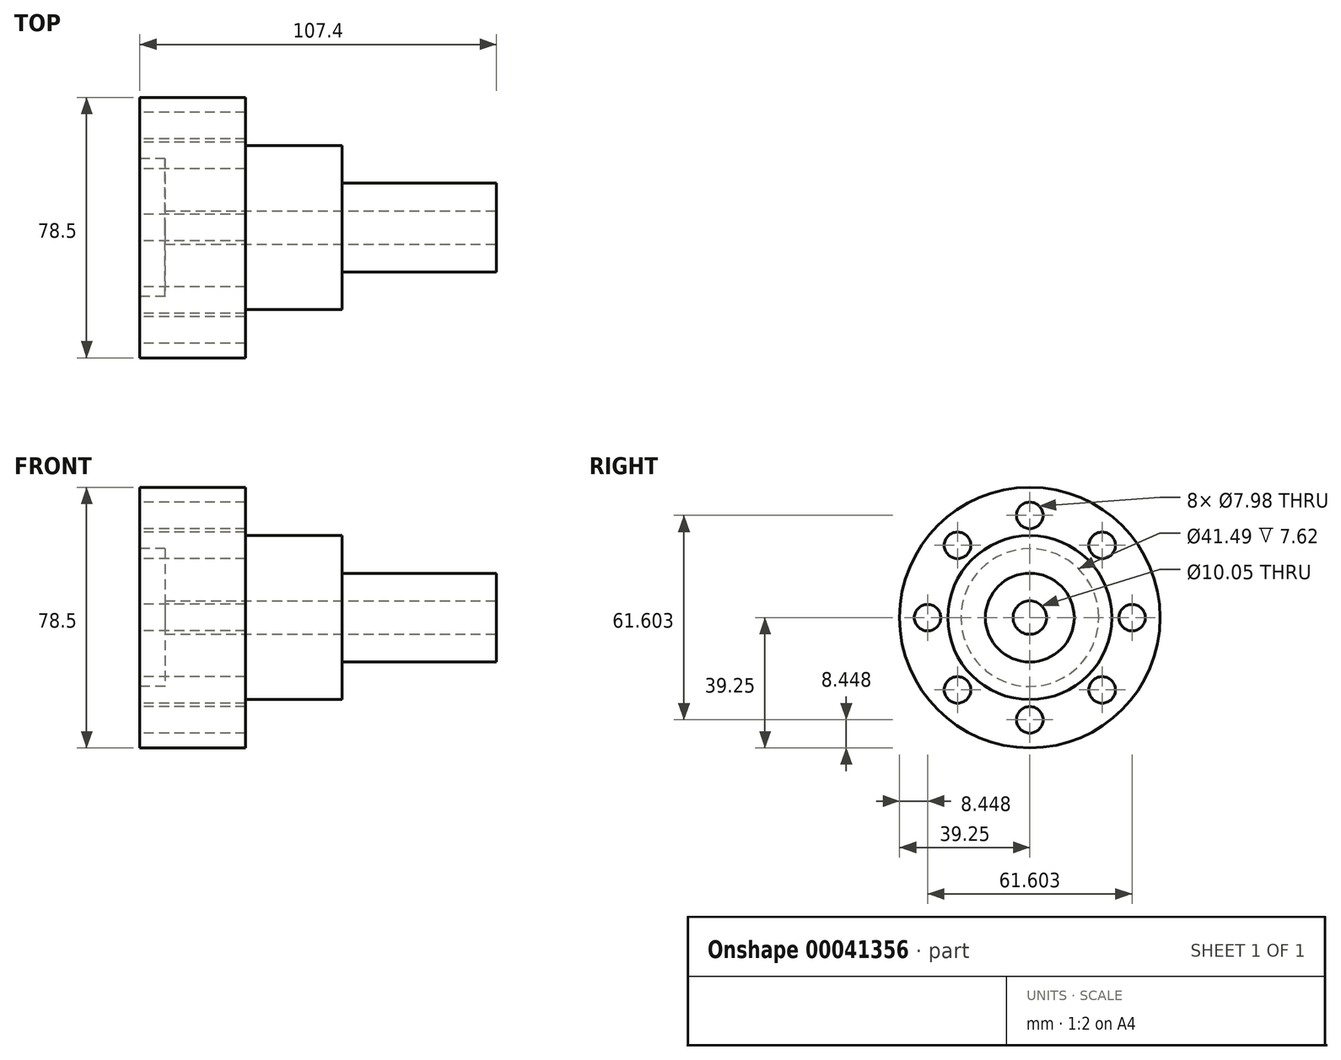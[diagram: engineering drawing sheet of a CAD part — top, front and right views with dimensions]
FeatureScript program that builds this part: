
annotation { "Feature Type Name" : "Feature", "Feature Type Description" : "" }
export const myFeature = defineFeature(function(context is Context, id is Id, definition is map)
    precondition{}
    {
        {
            var Q0;
            Q0=qCreatedBy(makeId("Front.planeOp"),FACE);
            var sketch = newSketch(context, id + "F0", { "sketchPlane" : qUnion([Q0])});
            skLineSegment(sketch, "E0", {"start": v(0, 0) * mm, "end": v(0, 39.25) * mm});
            skLineSegment(sketch, "E1", {"start": v(0, 39.25) * mm, "end": v(31.8, 39.25) * mm});
            skLineSegment(sketch, "E2", {"start": v(31.8, 39.25) * mm, "end": v(31.8, 24.7) * mm});
            skLineSegment(sketch, "E3", {"start": v(31.8, 24.7) * mm, "end": v(60.91, 24.7) * mm});
            skLineSegment(sketch, "E4", {"start": v(60.91, 24.7) * mm, "end": v(60.91, 13.38) * mm});
            skLineSegment(sketch, "E5", {"start": v(60.91, 13.38) * mm, "end": v(107.4, 13.38) * mm});
            skLineSegment(sketch, "E6", {"start": v(107.4, 13.38) * mm, "end": v(107.4, 0) * mm});
            skLineSegment(sketch, "E7", {"start": v(107.4, 0) * mm, "end": v(0, 0) * mm});
            skSolve(sketch);
        }
        {
            var Q0;
            Q0=makeQuery(id+"F0.imprint","IMPRINT",FACE,{"disambiguationData":[TD([[makeQuery(id+"F0.imprint","IMPRINT",EDGE,{"derivedFrom":sQuery(id+"F0.wireOp",EDGE,"E0")}),-1.0]])]});
            var Q1;
            Q1=sQuery(id+"F0.wireOp",EDGE,"E7");
            revolve(context, id + "F1", {"entities" : qUnion([Q0]), "axis" : qUnion([Q1]), "revolveType" : RevolveType.FULL});
        }
        {
            var Q0;
            Q0=makeQuery(id+"F1.opRevolve","SWEPT_FACE",FACE,{"disambiguationData":[OSD([sQuery(id+"F0.wireOp",EDGE,"E0")])]});
            var sketch = newSketch(context, id + "F2", { "sketchPlane" : qUnion([Q0])});
            skCircle(sketch, "E8", {"center": v(0, 0) * mm, "radius": 20.75 * mm});
            skSolve(sketch);
        }
        {
            var Q0;
            Q0=makeQuery(id+"F2.imprint","IMPRINT",FACE,{"disambiguationData":[TD([[makeQuery(id+"F2.imprint","IMPRINT",EDGE,{"derivedFrom":sQuery(id+"F2.wireOp",EDGE,"E8")}),1.0]])]});
            extrude(context, id + "F3", {"entities" : qUnion([Q0]), "operationType" : NewBodyOperationType.REMOVE, "oppositeDirection" : true, "depth" : 7.62 * mm});
        }
        {
            var Q0;
            Q0=makeQuery(id+"F1.opRevolve","SWEPT_FACE",FACE,{"disambiguationData":[OSD([sQuery(id+"F0.wireOp",EDGE,"E6")])]});
            var sketch = newSketch(context, id + "F4", { "sketchPlane" : qUnion([Q0])});
            skCircle(sketch, "E9", {"center": v(0, 0) * mm, "radius": 5.03 * mm});
            skSolve(sketch);
        }
        {
            var Q0;
            Q0=makeQuery(id+"F4.imprint","IMPRINT",FACE,{"disambiguationData":[TD([[makeQuery(id+"F4.imprint","IMPRINT",EDGE,{"derivedFrom":sQuery(id+"F4.wireOp",EDGE,"E9")}),1.0]])]});
            extrude(context, id + "F5", {"entities" : qUnion([Q0]), "operationType" : NewBodyOperationType.REMOVE, "endBound" : BoundingType.THROUGH_ALL, "oppositeDirection" : true, "depth" : 25.4 * mm});
        }
        {
            var Q0;
            Q0=makeQuery(id+"F1.opRevolve","SWEPT_FACE",FACE,{"disambiguationData":[OSD([sQuery(id+"F0.wireOp",EDGE,"E0")])]});
            var sketch = newSketch(context, id + "F6", { "sketchPlane" : qUnion([Q0])});
            skCircle(sketch, "E10", {"center": v(0, 0) * mm, "radius": 30.8 * mm, "construction": true});
            skCircle(sketch, "E11", {"center": v(0, 30.8) * mm, "radius": 3.99 * mm});
            skCircle(sketch, "E12.1.0", {"center": v(-21.78, 21.78) * mm, "radius": 3.99 * mm});
            skCircle(sketch, "E12.2.0", {"center": v(-30.8, 0) * mm, "radius": 3.99 * mm});
            skCircle(sketch, "E12.3.0", {"center": v(-21.78, -21.78) * mm, "radius": 3.99 * mm});
            skCircle(sketch, "E12.4.0", {"center": v(0, -30.8) * mm, "radius": 3.99 * mm});
            skCircle(sketch, "E12.5.0", {"center": v(21.78, -21.78) * mm, "radius": 3.99 * mm});
            skCircle(sketch, "E13.1.6.0", {"center": v(30.8, 0) * mm, "radius": 3.99 * mm});
            skCircle(sketch, "E13.1.7.0", {"center": v(21.78, 21.78) * mm, "radius": 3.99 * mm});
            skSolve(sketch);
        }
        {
            var Q0;
            Q0 = qSketchRegion(id + "F6", true);
            extrude(context, id + "F7", {"entities" : qUnion([Q0]), "operationType" : NewBodyOperationType.REMOVE, "endBound" : BoundingType.THROUGH_ALL, "oppositeDirection" : true, "depth" : 25.4 * mm});
        }
    });
